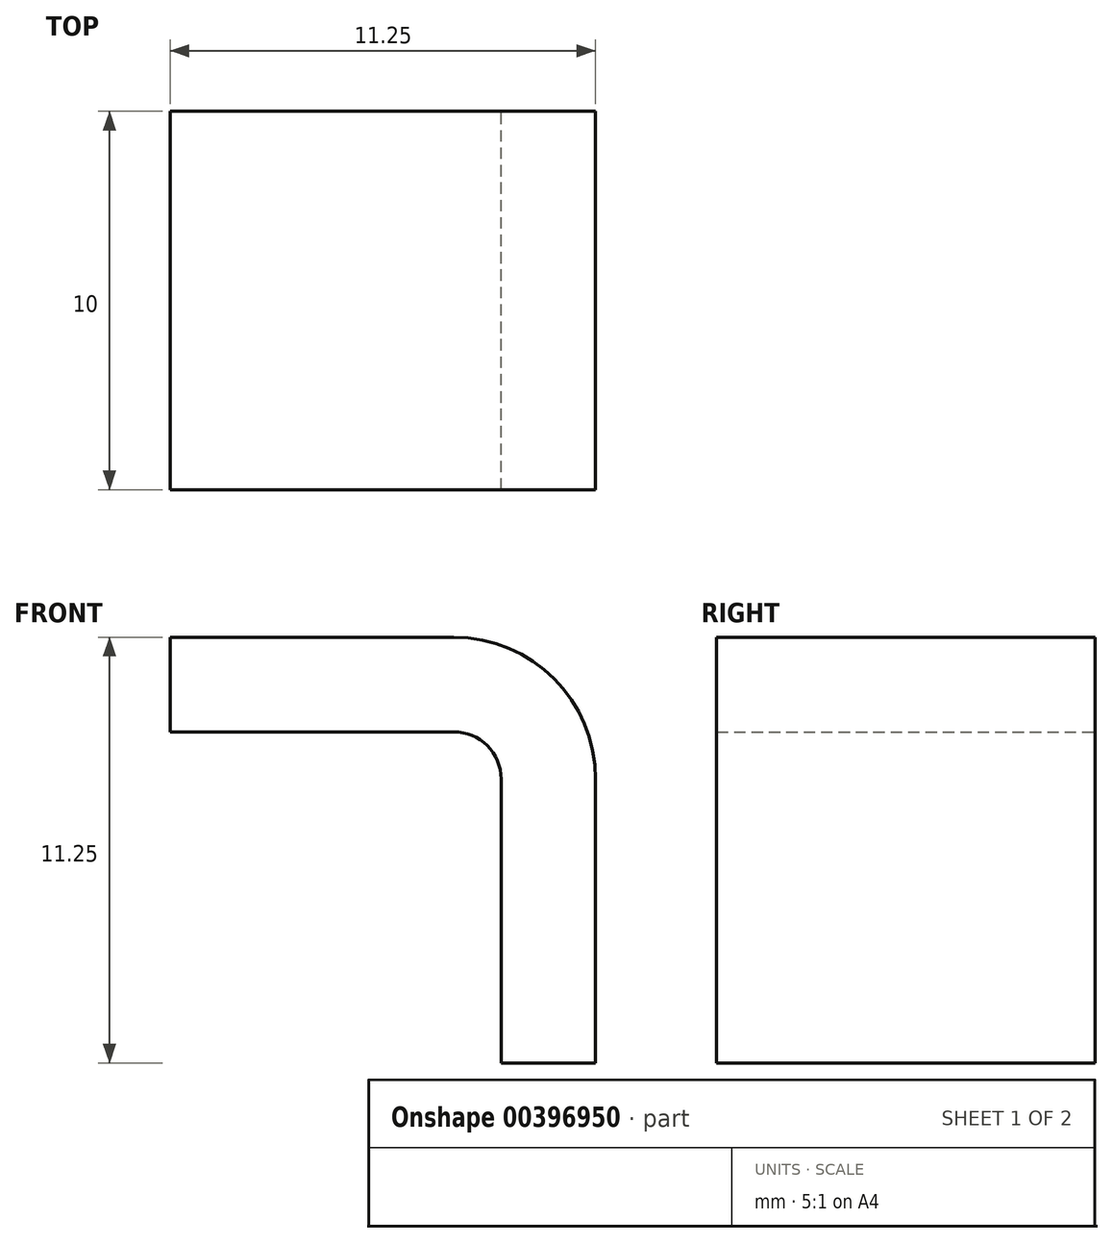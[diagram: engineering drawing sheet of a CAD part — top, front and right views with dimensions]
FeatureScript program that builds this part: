
annotation { "Feature Type Name" : "Feature", "Feature Type Description" : "" }
export const myFeature = defineFeature(function(context is Context, id is Id, definition is map)
    precondition{}
    {
        {
            var Q0;
            Q0=qCreatedBy(makeId("Front.planeOp"),FACE);
            var sketch = newSketch(context, id + "F0", { "sketchPlane" : qUnion([Q0])});
            skLineSegment(sketch, "E0", {"start": v(0, 0) * mm, "end": v(7.5, 0) * mm});
            skLineSegment(sketch, "E1", {"start": v(10, -2.5) * mm, "end": v(10, -10) * mm});
            skPoint(sketch, "E2.visualSharp", {"position": v(10, 0) * mm});
            skArc(sketch, "E2.filletArc", {"start": v(10, -2.5) * mm, "mid": v(9.27, -0.73) * mm, "end": v(7.5, 0) * mm});
            skSolve(sketch);
        }
        {
            var Q0;
            Q0=qCreatedBy(makeId("Right.planeOp"),FACE);
            var sketch = newSketch(context, id + "F1", { "sketchPlane" : qUnion([Q0])});
            skLineSegment(sketch, "E3.bottom", {"start": v(-5, -1.25) * mm, "end": v(5, -1.25) * mm});
            skLineSegment(sketch, "E3.top", {"start": v(-5, 1.25) * mm, "end": v(5, 1.25) * mm});
            skLineSegment(sketch, "E3.left", {"start": v(-5, -1.25) * mm, "end": v(-5, 1.25) * mm});
            skLineSegment(sketch, "E3.right", {"start": v(5, -1.25) * mm, "end": v(5, 1.25) * mm});
            skPoint(sketch, "E3.middle", {"position": v(0, 0) * mm});
            skSolve(sketch);
        }
        {
            var Q0;
            Q0=makeQuery(id+"F1.imprint","IMPRINT",FACE,{"disambiguationData":[TD([[makeQuery(id+"F1.imprint","IMPRINT",EDGE,{"derivedFrom":sQuery(id+"F1.wireOp",EDGE,"E3.bottom")}),1.0]])]});
            var Q1;
            Q1=sQuery(id+"F0.wireOp",EDGE,"E0");
            var Q2;
            Q2=sQuery(id+"F0.wireOp",EDGE,"E2.filletArc");
            var Q3;
            Q3=sQuery(id+"F0.wireOp",EDGE,"E1");
            sweep(context, id + "F2", {"profiles" : qUnion([Q0]), "path" : qUnion([Q1, Q2, Q3])});
        }
    });
